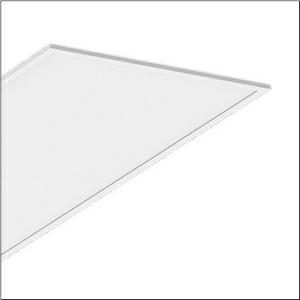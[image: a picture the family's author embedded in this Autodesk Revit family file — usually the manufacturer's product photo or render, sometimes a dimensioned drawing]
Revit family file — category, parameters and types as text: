
# Revit family: apollon_21_linear_51mq1awd2m14
name_source: partatom
category: Lighting Fixtures
units: mm (PartAtom-declared; Revit-internal decimal feet)

## family parameters
Cut with Voids When Loaded = No
Host = Face
Light Source = No
Part Type = Normal
Room Calculation Point = No
Round Connector Dimension = Use Diameter
Shared = No

## types (1)
- --- (1 x LED, 7000 lm, 44.5 W, 4000K)
    Apparent Load = 45 VA
    CIE Flux Codes = 60 87 97 100 100
    Color Rendering = 80
    Color Temperature = 4000K
    Default Elevation = 1800 mm
    Description = Apollon 21 linear, office luminaire, primary optical cover: micro prismatic cover, of PMMA, CAT 2 (L<= 3000cd/m²), light emission: direct distribution, primary light characteristic: symmetric, installation type: lay-in mounting, LED, rated luminous flux: 7.820lm, luminous efficacy: 173lm/W, light colour: 830/840, colour temperature: 3000/4000K, control gear: DALI 2, Multilumen, with terminal, 5-pole, mains connection: 220..240V, AC/DC, 0/50..60Hz, rated input power: 45.3W, suitable for self-contained emergency lighting element 59MQE002602A with integrated self-test function according to EN 60598-2-22, housing, of aluminium, coated, traffic white (RAL 9016), length: 1.195mm, width: 595mm, height: 55mm, recess depth: 180mm, housing upper side, of sheet steel, galvanised, protection rating (complete): IP20, protection rating (lamp compartment, on room side): IP50, insulation class (complete): insulation class II (safety insulation), certification: CE, ENEC, impact resistance: IK03, permissible operating ambient temperature: -20..+45°C, permissible storage temperature: -40..+80°C, standard: EN 60598-2-22, packaging unit: 1 piece
    Height = 0 mm  [stored 0 ft]
    Lamp = 1 x LED
    Lamp Light Flux = 7000 lm
    Lamp Power = 44.5 W
    Lamp count = 1
    Length = 1195 mm
    Luminous efficacy = 157 lm/W
    Manufacturer = Siteco
    ModVariant = No
    Model = 51MQ1AWD2M14
    Mounting Place = Ceiling
    Mounting Type = Recessed
    Number of Poles = 1
    OnlyDefault = Yes
    Power Factor = 1
    Product Name = Apollon 21 linear
    Product group = office luminaire | ceiling recessed
    ProductGroupID = 400
    Protection Class = Protection class II
    Protection Degree = IP 20
    RLX_Detail_Level = 1
    RLX_Emergency_Light_Flux = 0 lm
    RLX_Emergency_Type = 0
    RLX_Emergency_Type_DB = No
    RlxData = <blob elided: 19713 chars, md5=afb3e965>
    Socket = socket
    Standby Power = 0 W
    System Light Flux = 7000 lm
    System Power = 45 W
    Type Comments = factory setting
    Type Image = l_1335551.jpg
    URL = http://relux.com
    VarID = @adj_088687
    Voltage = 0 V
    Weight = 0.00 kg
    Width = 595 mm

note: [stored X ft] marks values corroborated as IEEE doubles in the binary element streams (Revit-internal decimal feet)

## geometry (parser evidence)
native form markers: Blend x4, Sweep x10
no freeform markers — native parametric forms only
